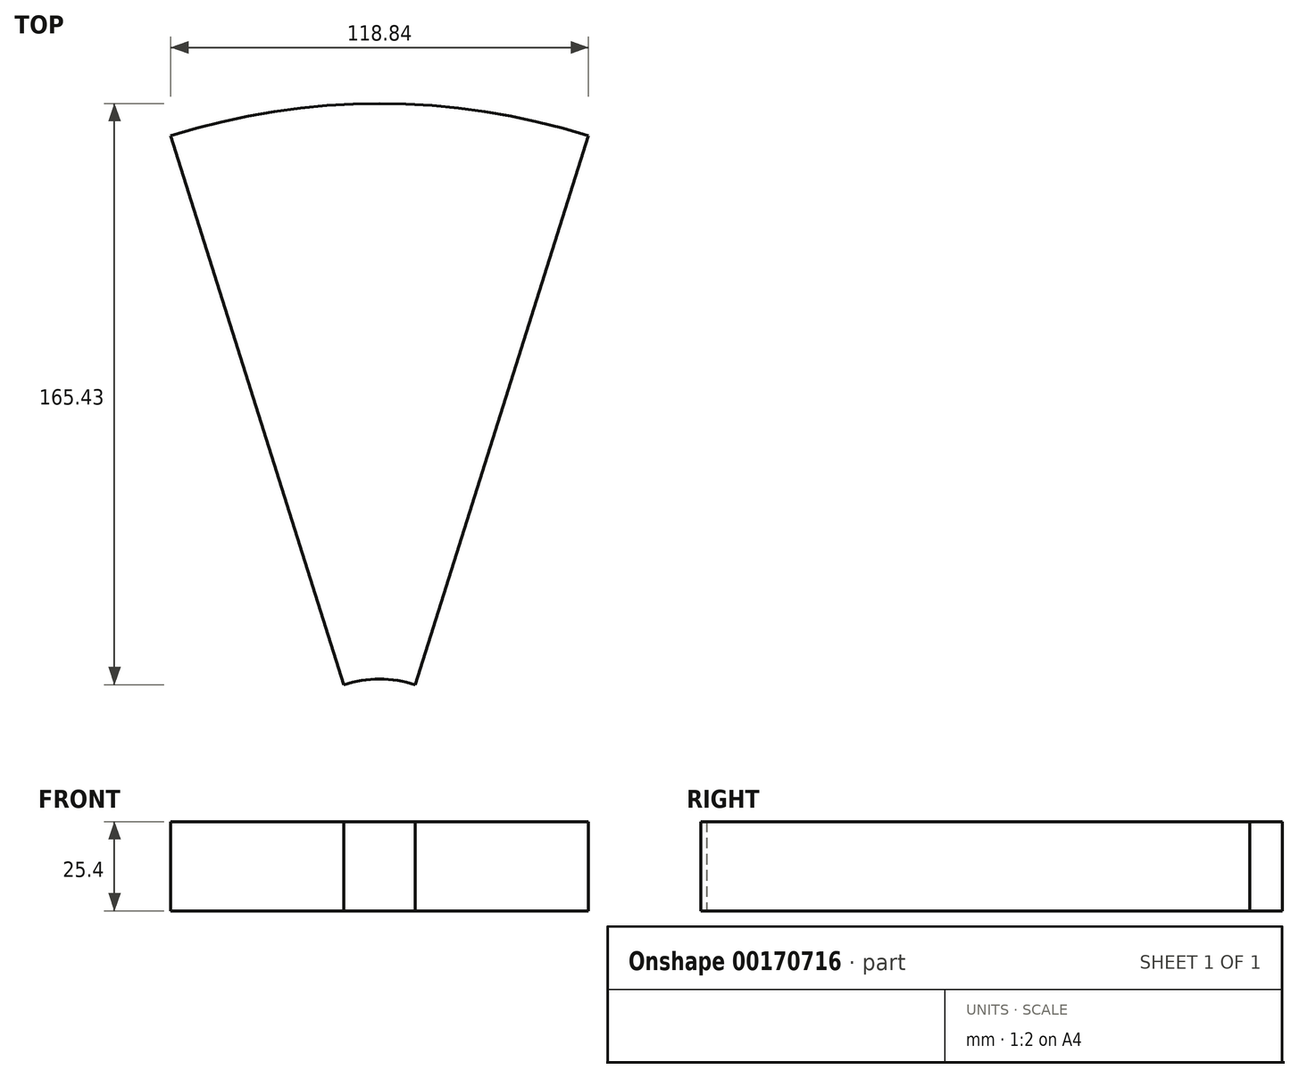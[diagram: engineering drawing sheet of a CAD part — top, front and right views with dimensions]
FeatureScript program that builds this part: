
annotation { "Feature Type Name" : "Feature", "Feature Type Description" : "" }
export const myFeature = defineFeature(function(context is Context, id is Id, definition is map)
    precondition{}
    {
        {
            var Q0;
            Q0=qCreatedBy(makeId("Top.planeOp"),FACE);
            var sketch = newSketch(context, id + "F0", { "sketchPlane" : qUnion([Q0])});
            skArc(sketch, "E0", {"start": v(10.16, 31.42) * mm, "mid": v(0, 33.02) * mm, "end": v(-10.16, 31.42) * mm});
            skArc(sketch, "E1", {"start": v(59.42, 187.67) * mm, "mid": v(0, 196.85) * mm, "end": v(-59.42, 187.67) * mm});
            skLineSegment(sketch, "E2", {"start": v(10.16, 31.42) * mm, "end": v(59.42, 187.67) * mm});
            skLineSegment(sketch, "E3", {"start": v(-59.42, 187.67) * mm, "end": v(-10.16, 31.42) * mm});
            skLineSegment(sketch, "E4", {"start": v(0, 0) * mm, "end": v(0, 96.4) * mm, "construction": true});
            skLineSegment(sketch, "E5", {"start": v(5.87, 38.93) * mm, "end": v(51.43, 183.43) * mm, "construction": true});
            skLineSegment(sketch, "E6", {"start": v(-51.43, 183.43) * mm, "end": v(-5.87, 38.93) * mm, "construction": true});
            skArc(sketch, "E7", {"start": v(-5.87, 38.93) * mm, "mid": v(0, 39.37) * mm, "end": v(5.87, 38.93) * mm, "construction": true});
            skArc(sketch, "E8", {"start": v(51.43, 183.43) * mm, "mid": v(0, 190.5) * mm, "end": v(-51.43, 183.43) * mm, "construction": true});
            skSolve(sketch);
        }
        {
            var Q0;
            Q0=makeQuery(id+"F0.imprint","IMPRINT",FACE,{"disambiguationData":[TD([[makeQuery(id+"F0.imprint","IMPRINT",EDGE,{"derivedFrom":sQuery(id+"F0.wireOp",EDGE,"E0")}),-1.0]])]});
            var Q1;
            Q1=makeQuery(id+"F0.imprint","IMPRINT",FACE,{"disambiguationData":[TD([[makeQuery(id+"F0.imprint","IMPRINT",EDGE,{"derivedFrom":sQuery(id+"F0.wireOp",EDGE,"E5")}),1.0]])]});
            extrude(context, id + "F1", {"entities" : qUnion([Q0, Q1]), "depth" : 25.4 * mm});
        }
    });
